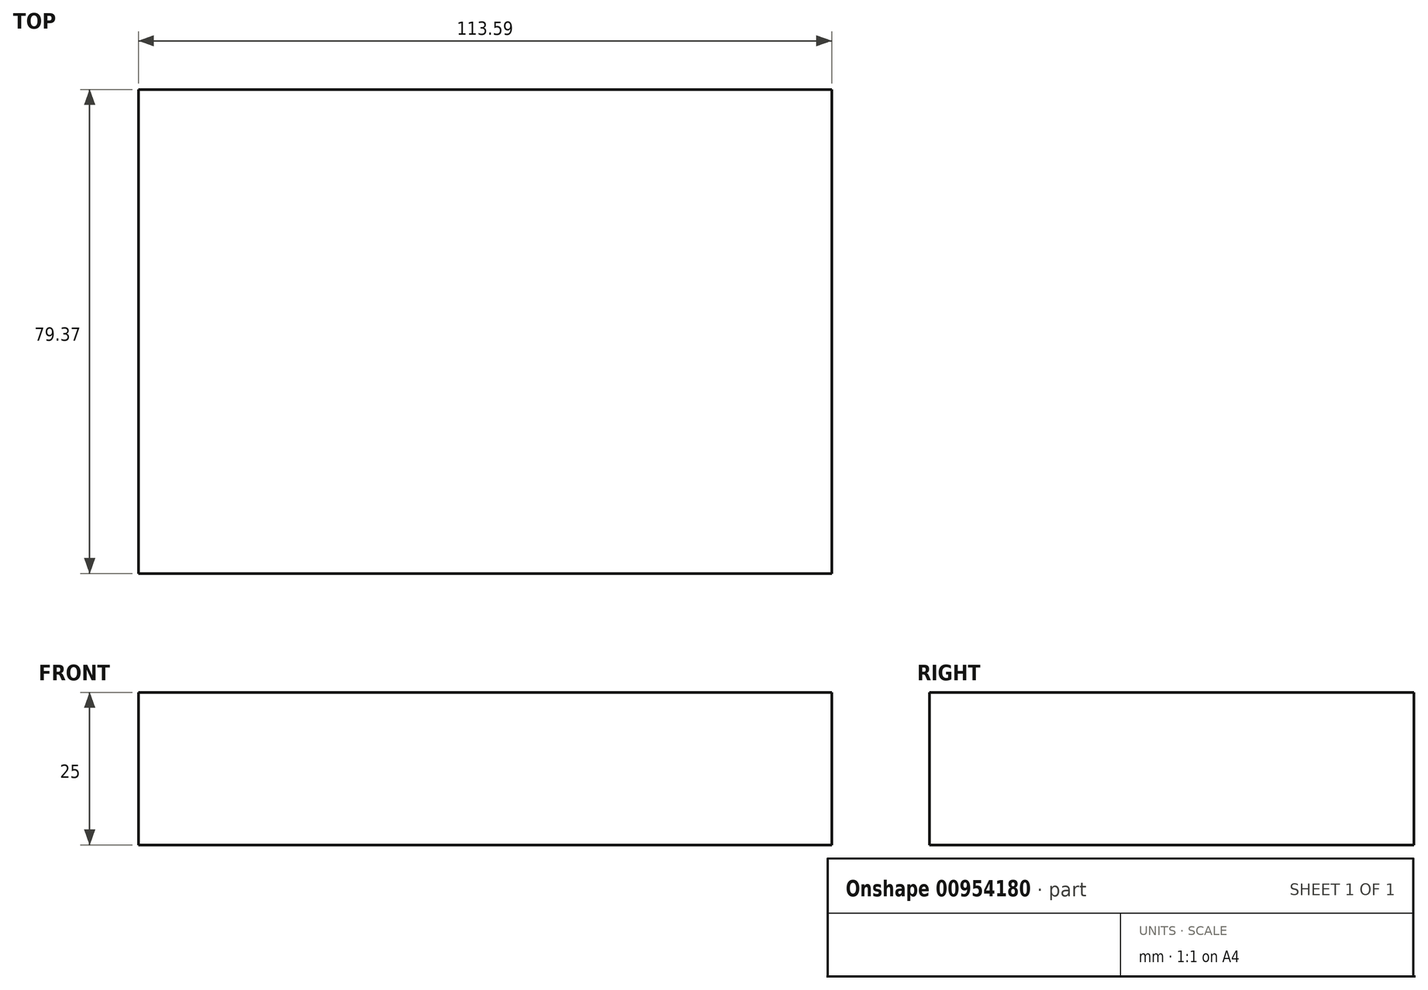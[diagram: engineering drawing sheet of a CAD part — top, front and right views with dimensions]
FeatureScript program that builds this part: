
annotation { "Feature Type Name" : "Feature", "Feature Type Description" : "" }
export const myFeature = defineFeature(function(context is Context, id is Id, definition is map)
    precondition{}
    {
        {
            var Q0;
            Q0=qCreatedBy(makeId("Top.planeOp"),FACE);
            var sketch = newSketch(context, id + "F0", { "sketchPlane" : qUnion([Q0])});
            skLineSegment(sketch, "E0.bottom", {"start": v(58.48, 37.48) * mm, "end": v(-55.11, 37.48) * mm});
            skLineSegment(sketch, "E0.top", {"start": v(58.48, -41.89) * mm, "end": v(-55.11, -41.89) * mm});
            skLineSegment(sketch, "E0.left", {"start": v(58.48, 37.48) * mm, "end": v(58.48, -41.89) * mm});
            skLineSegment(sketch, "E0.right", {"start": v(-55.11, 37.48) * mm, "end": v(-55.11, -41.89) * mm});
            skSolve(sketch);
        }
        {
            var Q0;
            Q0=makeQuery(id+"F0.imprint","IMPRINT",FACE,{"disambiguationData":[TD([[makeQuery(id+"F0.imprint","IMPRINT",EDGE,{"derivedFrom":sQuery(id+"F0.wireOp",EDGE,"E0.bottom")}),1.0]])]});
            extrude(context, id + "F1", {"entities" : qUnion([Q0]), "depth" : 25 * mm, "offsetDistance" : 25 * mm});
        }
    });
